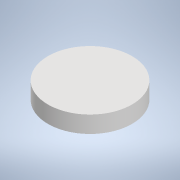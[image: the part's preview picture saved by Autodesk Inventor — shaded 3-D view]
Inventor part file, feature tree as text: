
AUTODESK INVENTOR PART (.ipt)
format: ipt  version: 2022 (Build 260153000, 153)  size: 90,624 bytes
history: native  units: mm
features: extrude x1, sketch x1
ambient origin geometry x8: Origin, YZ Plane, XZ Plane, XY Plane, X Axis, Y Axis, Z Axis, Center Point
bodies: Solid1 (feature_tree)
feature tree (2):
  extrude  "Extrusion1"  Depth=5.0mm TaperAngle=0.0deg
  sketch  "Sketch1"  dims[d0=25.0mm d1=5.0mm d2=0.0mm]
